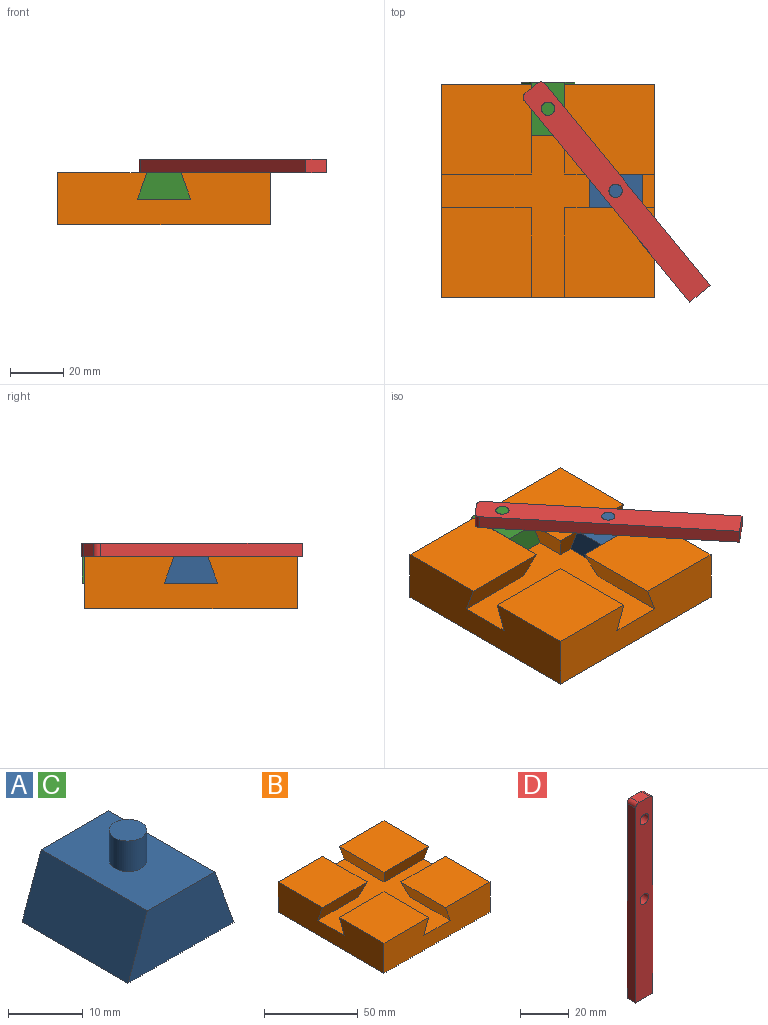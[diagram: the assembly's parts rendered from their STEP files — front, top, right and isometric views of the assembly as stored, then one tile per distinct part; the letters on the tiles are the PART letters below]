
ASSEMBLY  parts=4 mates=4
PART A: 8 faces, bbox 20x20x15 mm
  f0: plane 20x12.72mm, normal (0,0,1), area 234.8mm2, adj f1,f3,f4,f5,f6
  f1: plane 20x10mm, normal (-0.94,0,0.34), area 212.8mm2, adj f0,f2,f4,f5
  f2: plane 20x20mm, normal (0,0,-1), area 400mm2, adj f1,f3,f4,f5
  f3: plane 20x10mm, normal (0.94,0,0.34), area 212.8mm2, adj f0,f2,f4,f5
  f4: plane 20x10mm, normal (0,-1,0), area 163.6mm2, adj f0,f1,f2,f3
  f5: plane 20x10mm, normal (0,1,0), area 163.6mm2, adj f0,f1,f2,f3
  f6: cylinder r=2.5mm len=5mm, axis (0,0,-1), area 78.5mm2, adj f0,f7
  f7: plane 5x5mm, normal (0,0,1), area 19.6mm2, adj f6
PART B: 18 faces, bbox 80x80x19.6 mm
  f0: plane 33.64x33.64mm, normal (0,0,1), area 1131.6mm2, adj f2,f5,f12,f16
  f1: plane 33.64x33.64mm, normal (0,0,1), area 1131.6mm2, adj f9,f11,f13,f14
  f2: plane 33.64x10mm, normal (-0.94,0,-0.34), area 338.6mm2, adj f0,f8,f12,f16
  f3: plane 33.64x10mm, normal (0.94,0,-0.34), area 338.6mm2, adj f8,f10,f12,f15
  f4: plane 80x80mm, normal (0,0,-1), area 6400mm2, adj f5,f11,f12,f13
  f5: plane 80x19.63mm, normal (1,0,0), area 1406.5mm2, adj f0,f4,f6,f8,f12,f13,f16,f17
  f6: plane 33.64x33.64mm, normal (0,0,1), area 1131.6mm2, adj f5,f7,f13,f17
  f7: plane 33.64x10mm, normal (-0.94,0,-0.34), area 338.6mm2, adj f6,f8,f13,f17
  f8: plane 80x80mm, normal (0,0,1), area 2800mm2, adj f2,f3,f5,f7,f9,f11,f12,f13
  f9: plane 33.64x10mm, normal (0.94,0,-0.34), area 338.6mm2, adj f1,f8,f13,f14
  f10: plane 33.64x33.64mm, normal (0,0,1), area 1131.6mm2, adj f3,f11,f12,f15
  f11: plane 80x19.63mm, normal (-1,0,0), area 1406.5mm2, adj f1,f4,f8,f10,f12,f13,f14,f15
  f12: plane 80x19.63mm, normal (0,1,0), area 1406.5mm2, adj f0,f2,f3,f4,f5,f8,f10,f11
  f13: plane 80x19.63mm, normal (0,-1,0), area 1406.5mm2, adj f1,f4,f5,f6,f7,f8,f9,f11
  f14: plane 33.64x10mm, normal (0,0.94,-0.34), area 338.6mm2, adj f1,f8,f9,f11
  f15: plane 33.64x10mm, normal (0,-0.94,-0.34), area 338.6mm2, adj f3,f8,f10,f11
  f16: plane 33.64x10mm, normal (0,-0.94,-0.34), area 338.6mm2, adj f0,f2,f5,f8
  f17: plane 33.64x10mm, normal (0,0.94,-0.34), area 338.6mm2, adj f5,f6,f7,f8
PART C: same geometry as A
PART D: 10 faces, bbox 10x5x100 mm
  f0: plane 98x5mm, normal (1,0,0), area 490mm2, adj f1,f7,f8,f9
  f1: cylinder r=2mm len=5mm, axis (0,1,0), area 15.7mm2, adj f0,f2,f8,f9
  f2: plane 6x5mm, normal (0,0,1), area 30mm2, adj f1,f3,f8,f9
  f3: cylinder r=2mm len=5mm, axis (0,1,0), area 15.7mm2, adj f2,f4,f8,f9
  f4: plane 98x5mm, normal (-1,0,0), area 490mm2, adj f3,f7,f8,f9
  f5: cylinder r=2.5mm len=5mm, axis (0,1,0), area 78.5mm2, adj f8,f9
  f6: cylinder r=2.5mm len=5mm, axis (0,1,0), area 78.5mm2, adj f8,f9
  f7: plane 10x5mm, normal (0,0,-1), area 50mm2, adj f0,f4,f8,f9
  f8: plane 100x10mm, normal (0,-1,0), area 959mm2, adj f0,f1,f2,f3,f4,f5,f6,f7
  f9: plane 100x10mm, normal (0,1,0), area 959mm2, adj f0,f1,f2,f3,f4,f5,f6,f7
PLACE A rot(axis=(0,0,1),90deg) t=(-108.97,-50.79,68.74)mm
PLACE B rot(axis=(0,0,1),0deg) t=(-114.38,-100.79,68.74)mm fixed
PLACE C t=(-114.38,-19.9,68.74)mm
PLACE D rot(axis=(-0.89,-0.32,0.32),96.5deg) t=(-71.07,-102.58,78.74)mm
MATE revolute A.f6 <-> D.f5  axis (0,0,1) through (-98.97,-60.79,83.74)mm
MATE revolute C.f6 <-> D.f6  axis (0,0,1) through (-124.38,-29.9,83.74)mm
MATE slider C.f4 <-> B.f13  axis (0,-1,0) through (-124.38,-39.9,68.74)mm
MATE slider A.f4 <-> B.f5  axis (1,0,0) through (-88.97,-60.79,68.74)mm
